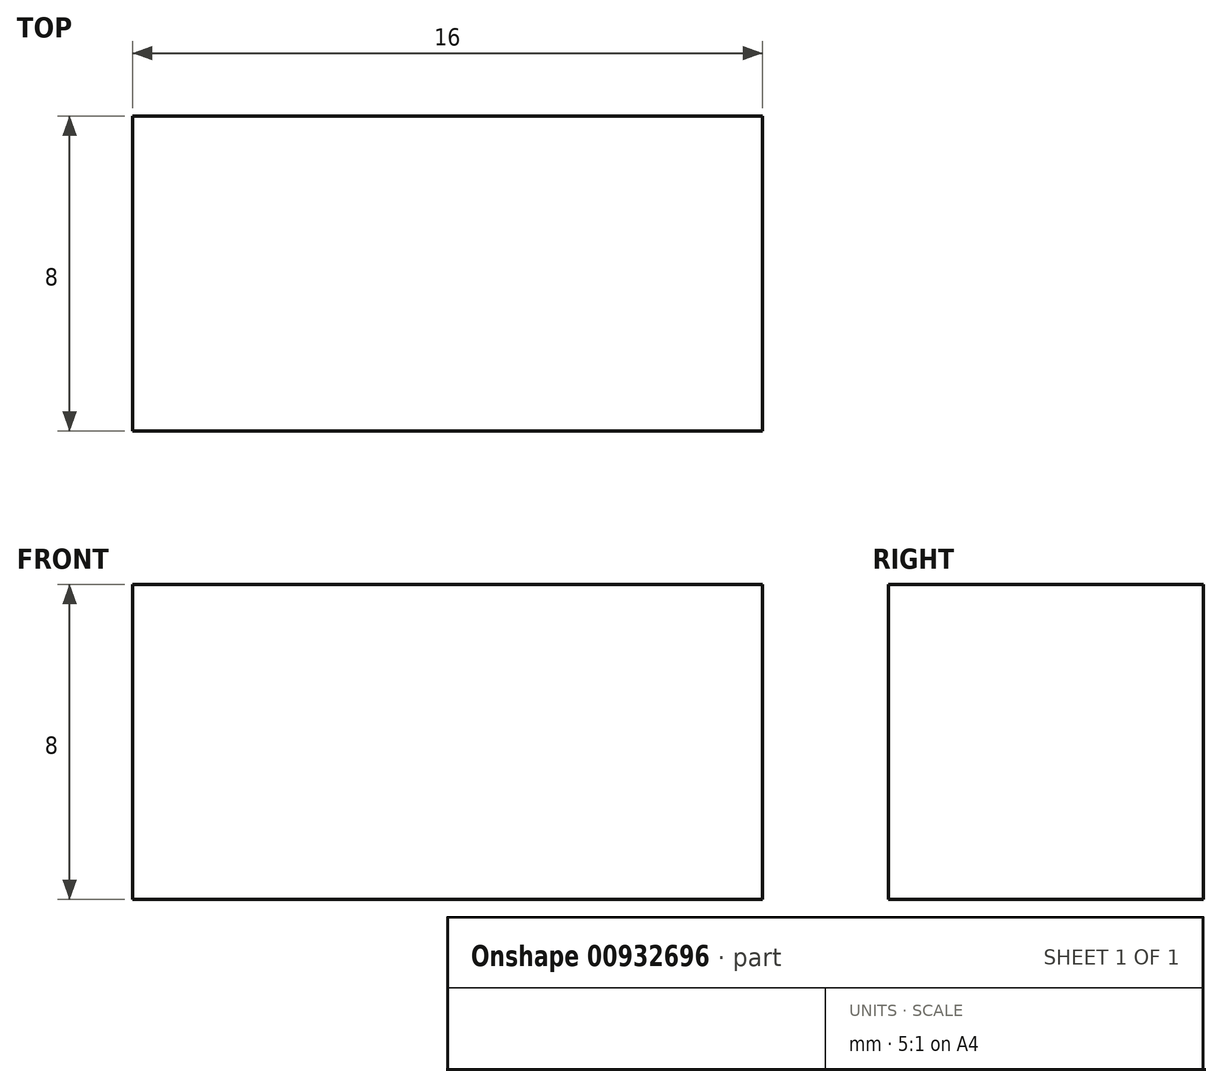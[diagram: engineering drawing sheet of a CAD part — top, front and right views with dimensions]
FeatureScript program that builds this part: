
annotation { "Feature Type Name" : "Feature", "Feature Type Description" : "" }
export const myFeature = defineFeature(function(context is Context, id is Id, definition is map)
    precondition{}
    {
        {
            var Q0;
            Q0=qCreatedBy(makeId("Top.planeOp"),FACE);
            var sketch = newSketch(context, id + "F0", { "sketchPlane" : qUnion([Q0])});
            skLineSegment(sketch, "E0.bottom", {"start": v(-8, 4) * mm, "end": v(8, 4) * mm});
            skLineSegment(sketch, "E0.top", {"start": v(-8, -4) * mm, "end": v(8, -4) * mm});
            skLineSegment(sketch, "E0.left", {"start": v(-8, 4) * mm, "end": v(-8, -4) * mm});
            skLineSegment(sketch, "E0.right", {"start": v(8, 4) * mm, "end": v(8, -4) * mm});
            skSolve(sketch);
        }
        {
            var Q0;
            Q0 = qSketchRegion(id + "F0", true);
            extrude(context, id + "F1", {"entities" : qUnion([Q0]), "depth" : 8 * mm, "offsetDistance" : 25 * mm});
        }
    });
